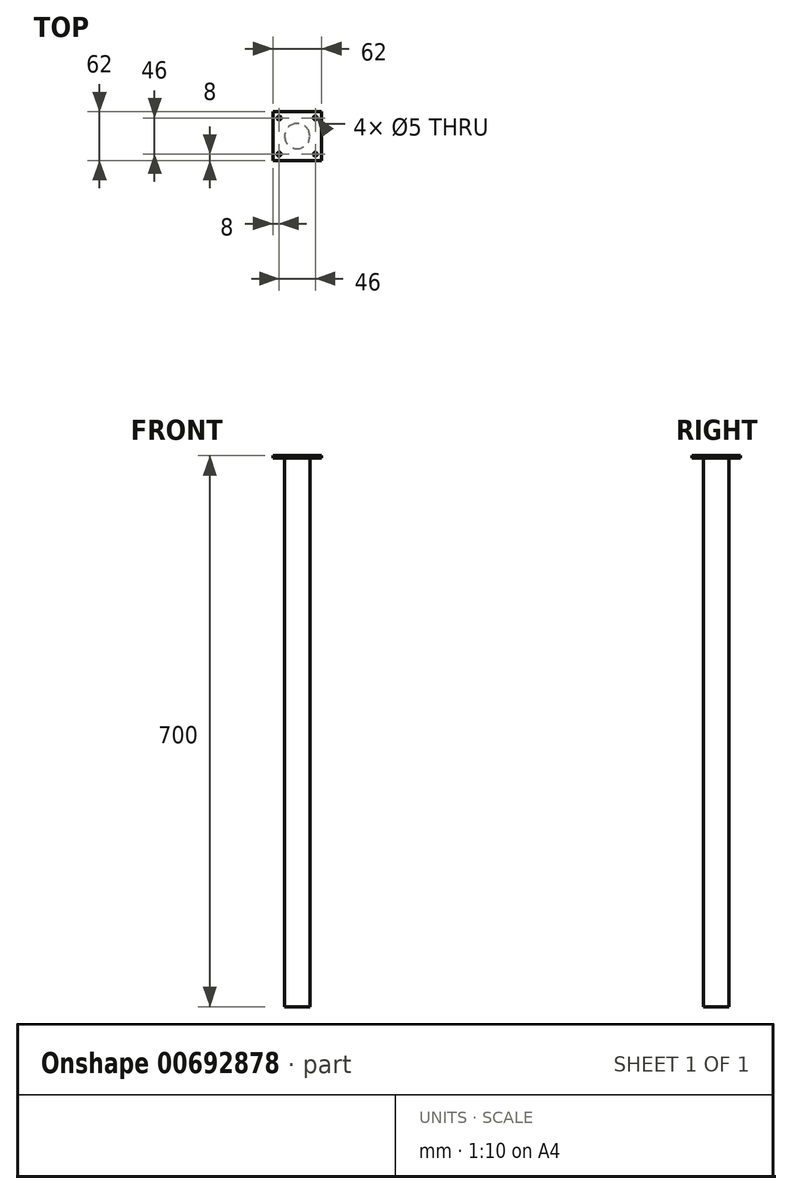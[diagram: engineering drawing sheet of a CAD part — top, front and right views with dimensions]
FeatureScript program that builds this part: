
annotation { "Feature Type Name" : "Feature", "Feature Type Description" : "" }
export const myFeature = defineFeature(function(context is Context, id is Id, definition is map)
    precondition{}
    {
        {
            var Q0;
            Q0=qCreatedBy(makeId("Top.planeOp"),FACE);
            var sketch = newSketch(context, id + "F0", { "sketchPlane" : qUnion([Q0])});
            skCircle(sketch, "E0", {"center": v(0, 0) * mm, "radius": 16 * mm});
            skSolve(sketch);
        }
        {
            var Q0;
            Q0 = qSketchRegion(id + "F0", true);
            extrude(context, id + "F1", {"entities" : qUnion([Q0]), "oppositeDirection" : true, "depth" : 700 * mm, "offsetDistance" : 25 * mm});
        }
        {
            var Q0;
            Q0=qCreatedBy(makeId("Top.planeOp"),FACE);
            var sketch = newSketch(context, id + "F2", { "sketchPlane" : qUnion([Q0])});
            skLineSegment(sketch, "E1.bottom", {"start": v(31, 31) * mm, "end": v(-31, 31) * mm});
            skLineSegment(sketch, "E1.top", {"start": v(31, -31) * mm, "end": v(-31, -31) * mm});
            skLineSegment(sketch, "E1.left", {"start": v(31, 31) * mm, "end": v(31, -31) * mm});
            skLineSegment(sketch, "E1.right", {"start": v(-31, 31) * mm, "end": v(-31, -31) * mm});
            skPoint(sketch, "E1.middle", {"position": v(0, 0) * mm});
            skSolve(sketch);
        }
        {
            var Q0;
            Q0 = qSketchRegion(id + "F2", true);
            extrude(context, id + "F3", {"entities" : qUnion([Q0]), "operationType" : NewBodyOperationType.ADD, "oppositeDirection" : true, "depth" : 3 * mm, "offsetDistance" : 25 * mm});
        }
        {
            var Q0;
            Q0=qCreatedBy(makeId("Top.planeOp"),FACE);
            var sketch = newSketch(context, id + "F4", { "sketchPlane" : qUnion([Q0])});
            skLineSegment(sketch, "E2.bottom", {"start": v(-23, 23) * mm, "end": v(23, 23) * mm, "construction": true});
            skLineSegment(sketch, "E2.top", {"start": v(-23, -23) * mm, "end": v(23, -23) * mm, "construction": true});
            skLineSegment(sketch, "E2.left", {"start": v(-23, 23) * mm, "end": v(-23, -23) * mm, "construction": true});
            skLineSegment(sketch, "E2.right", {"start": v(23, 23) * mm, "end": v(23, -23) * mm, "construction": true});
            skPoint(sketch, "E2.middle", {"position": v(0, 0) * mm});
            skCircle(sketch, "E3", {"center": v(-23, 23) * mm, "radius": 2.5 * mm});
            skCircle(sketch, "E4", {"center": v(23, 23) * mm, "radius": 2.5 * mm});
            skCircle(sketch, "E5", {"center": v(23, -23) * mm, "radius": 2.5 * mm});
            skCircle(sketch, "E6", {"center": v(-23, -23) * mm, "radius": 2.5 * mm});
            skSolve(sketch);
        }
        {
            var Q0;
            Q0 = qSketchRegion(id + "F4", true);
            extrude(context, id + "F5", {"entities" : qUnion([Q0]), "operationType" : NewBodyOperationType.REMOVE, "endBound" : BoundingType.UP_TO_NEXT, "oppositeDirection" : true, "depth" : 25 * mm, "offsetDistance" : 25 * mm});
        }
    });
